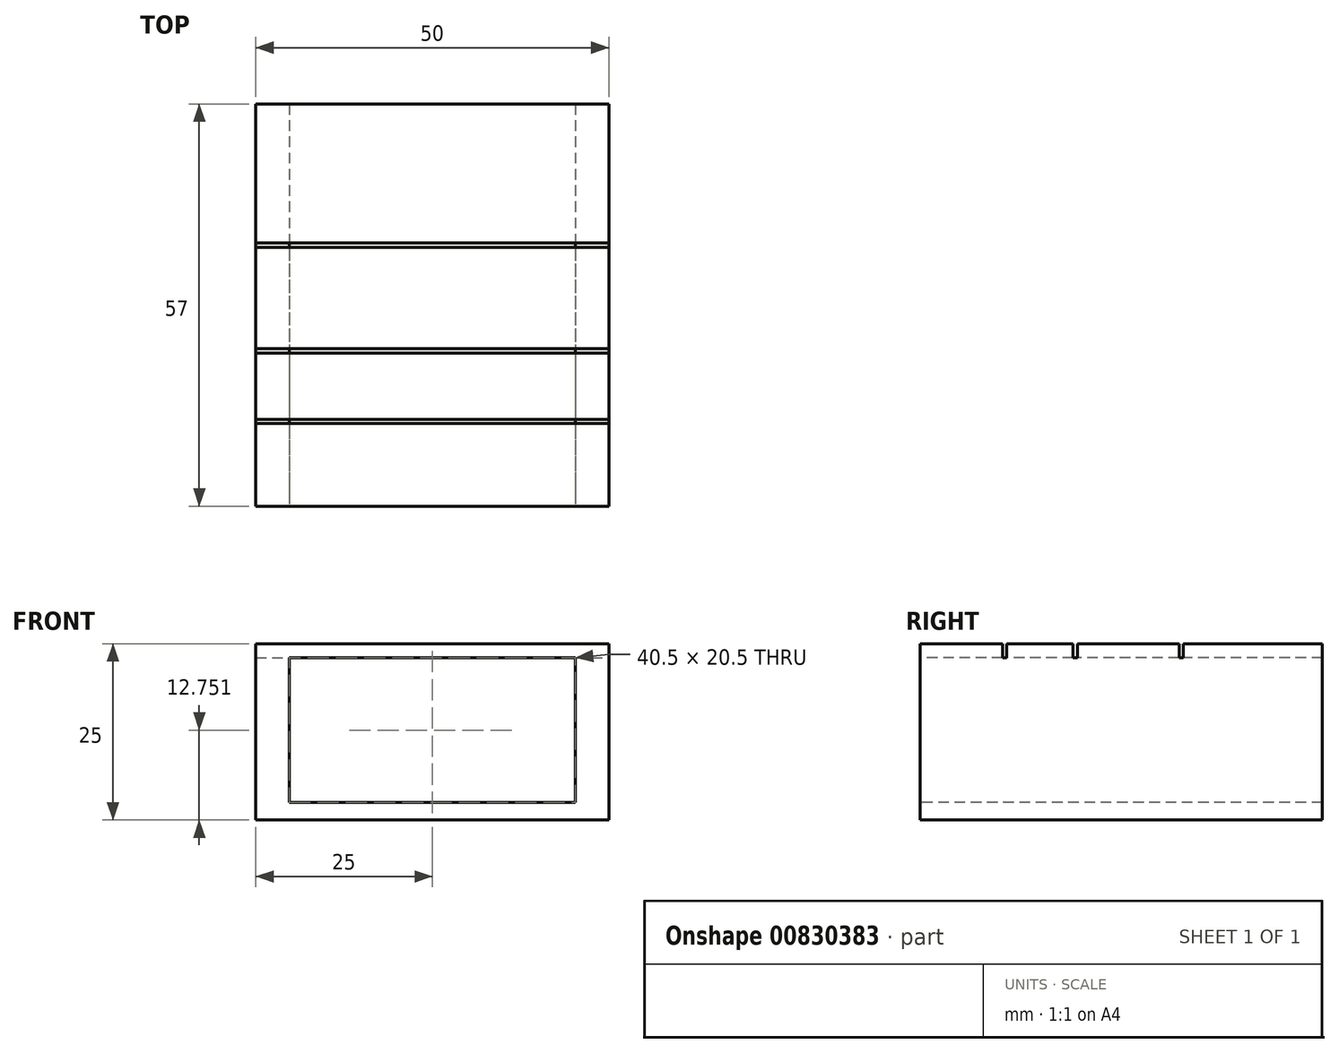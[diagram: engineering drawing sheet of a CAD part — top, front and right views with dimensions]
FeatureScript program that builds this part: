
annotation { "Feature Type Name" : "Feature", "Feature Type Description" : "" }
export const myFeature = defineFeature(function(context is Context, id is Id, definition is map)
    precondition{}
    {
        {
            var Q0;
            Q0=qCreatedBy(makeId("Right.planeOp"),FACE);
            var sketch = newSketch(context, id + "F0", { "sketchPlane" : qUnion([Q0])});
            skLineSegment(sketch, "E0.top", {"start": v(-45.07, 8.83) * mm, "end": v(11.93, 8.83) * mm, "construction": true});
            skLineSegment(sketch, "E0.left", {"start": v(-45.07, 33.83) * mm, "end": v(-45.07, 8.83) * mm, "construction": true});
            skLineSegment(sketch, "E0.right", {"start": v(11.93, 33.83) * mm, "end": v(11.93, 8.83) * mm, "construction": true});
            skLineSegment(sketch, "E1", {"start": v(-45.07, 33.83) * mm, "end": v(-33.07, 33.83) * mm, "construction": true});
            skLineSegment(sketch, "E2", {"start": v(-33.07, 33.83) * mm, "end": v(-23.07, 33.83) * mm, "construction": true});
            skLineSegment(sketch, "E3", {"start": v(-23.07, 33.83) * mm, "end": v(-8.07, 33.83) * mm, "construction": true});
            skLineSegment(sketch, "E4", {"start": v(-8.07, 33.83) * mm, "end": v(11.93, 33.83) * mm, "construction": true});
            skLineSegment(sketch, "E5", {"start": v(-45.07, 31.83) * mm, "end": v(11.93, 31.83) * mm, "construction": true});
            skSolve(sketch);
        }
        {
            var Q0;
            Q0=qCreatedBy(makeId("Right.planeOp"),FACE);
            var sketch = newSketch(context, id + "F1", { "sketchPlane" : qUnion([Q0])});
            skLineSegment(sketch, "E6.bottom", {"start": v(-33.37, 33.83) * mm, "end": v(-32.77, 33.83) * mm});
            skLineSegment(sketch, "E6.top", {"start": v(-33.37, 31.83) * mm, "end": v(-32.77, 31.83) * mm});
            skLineSegment(sketch, "E6.left", {"start": v(-33.37, 33.83) * mm, "end": v(-33.37, 31.83) * mm});
            skLineSegment(sketch, "E6.right", {"start": v(-32.77, 33.83) * mm, "end": v(-32.77, 31.83) * mm});
            skLineSegment(sketch, "E7.bottom", {"start": v(-45.07, 33.83) * mm, "end": v(11.93, 33.83) * mm});
            skLineSegment(sketch, "E7.top", {"start": v(-45.07, 8.83) * mm, "end": v(11.93, 8.83) * mm});
            skLineSegment(sketch, "E7.left", {"start": v(-45.07, 33.83) * mm, "end": v(-45.07, 8.83) * mm});
            skLineSegment(sketch, "E7.right", {"start": v(11.93, 33.83) * mm, "end": v(11.93, 8.83) * mm});
            skLineSegment(sketch, "E8.bottom", {"start": v(-23.37, 33.83) * mm, "end": v(-22.77, 33.83) * mm});
            skLineSegment(sketch, "E8.top", {"start": v(-23.37, 31.83) * mm, "end": v(-22.77, 31.83) * mm});
            skLineSegment(sketch, "E8.left", {"start": v(-23.37, 33.83) * mm, "end": v(-23.37, 31.83) * mm});
            skLineSegment(sketch, "E8.right", {"start": v(-22.77, 33.83) * mm, "end": v(-22.77, 31.83) * mm});
            skLineSegment(sketch, "E9.bottom", {"start": v(-8.37, 33.83) * mm, "end": v(-7.77, 33.83) * mm});
            skLineSegment(sketch, "E9.top", {"start": v(-8.37, 31.83) * mm, "end": v(-7.77, 31.83) * mm});
            skLineSegment(sketch, "E9.left", {"start": v(-8.37, 33.83) * mm, "end": v(-8.37, 31.83) * mm});
            skLineSegment(sketch, "E9.right", {"start": v(-7.77, 33.83) * mm, "end": v(-7.77, 31.83) * mm});
            skSolve(sketch);
        }
        {
            var Q0;
            Q0=makeQuery(id+"F1.imprint","IMPRINT",FACE,{"disambiguationData":[TD([[makeQuery(id+"F1.imprint","IMPRINT",EDGE,{"derivedFrom":sQuery(id+"F1.wireOp",EDGE,"E6.top")}),-1.0]])]});
            extrude(context, id + "F2", {"entities" : qUnion([Q0]), "oppositeDirection" : true, "depth" : 50 * mm, "offsetDistance" : 25 * mm});
        }
        {
            var Q0;
            Q0=makeQuery(id+"F2.opExtrude","SWEPT_FACE",FACE,{"disambiguationData":[OSD([sQuery(id+"F1.wireOp",EDGE,"E7.left")])]});
            var sketch = newSketch(context, id + "F3", { "sketchPlane" : qUnion([Q0])});
            skLineSegment(sketch, "E10.bottom", {"start": v(-45.25, 31.83) * mm, "end": v(-4.75, 31.83) * mm});
            skLineSegment(sketch, "E10.top", {"start": v(-45.25, 11.33) * mm, "end": v(-4.75, 11.33) * mm});
            skLineSegment(sketch, "E10.left", {"start": v(-45.25, 31.83) * mm, "end": v(-45.25, 11.33) * mm});
            skLineSegment(sketch, "E10.right", {"start": v(-4.75, 31.83) * mm, "end": v(-4.75, 11.33) * mm});
            skLineSegment(sketch, "E11", {"start": v(-25, 33.83) * mm, "end": v(-25, 31.83) * mm, "construction": true});
            skPoint(sketch, "E11.endSnap0", {"position": v(-25, 31.83) * mm});
            skSolve(sketch);
        }
        {
            var Q0;
            Q0=makeQuery(id+"F3.imprint","IMPRINT",FACE,{"disambiguationData":[TD([[makeQuery(id+"F3.imprint","IMPRINT",EDGE,{"derivedFrom":sQuery(id+"F3.wireOp",EDGE,"E10.bottom")}),-1.0]])]});
            var Q1;
            Q1=makeQuery(id+"F2.opExtrude","SWEPT_FACE",FACE,{"disambiguationData":[OSD([sQuery(id+"F1.wireOp",EDGE,"E7.right")])]});
            var Q2;
            Q2=makeQuery(id+"F2.opExtrude","SWEPT_BODY",BODY,{"disambiguationData":[OSD([sQuery(id+"F1.wireOp",EDGE,"E6.top"),sQuery(id+"F1.wireOp",EDGE,"E6.left"),sQuery(id+"F1.wireOp",EDGE,"E6.right"),sQuery(id+"F1.wireOp",EDGE,"E7.bottom"),sQuery(id+"F1.wireOp",EDGE,"E7.top"),sQuery(id+"F1.wireOp",EDGE,"E7.left"),sQuery(id+"F1.wireOp",EDGE,"E7.right"),sQuery(id+"F1.wireOp",EDGE,"E8.top"),sQuery(id+"F1.wireOp",EDGE,"E8.left"),sQuery(id+"F1.wireOp",EDGE,"E8.right"),sQuery(id+"F1.wireOp",EDGE,"E9.top"),sQuery(id+"F1.wireOp",EDGE,"E9.left"),sQuery(id+"F1.wireOp",EDGE,"E9.right")])]});
            extrude(context, id + "F4", {"entities" : qUnion([Q0]), "operationType" : NewBodyOperationType.REMOVE, "endBound" : BoundingType.UP_TO_SURFACE, "oppositeDirection" : true, "depth" : 25 * mm, "endBoundEntityFace" : qUnion([Q1]), "endBoundEntityBody" : qUnion([Q2]), "offsetDistance" : 25 * mm});
        }
    });
